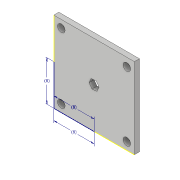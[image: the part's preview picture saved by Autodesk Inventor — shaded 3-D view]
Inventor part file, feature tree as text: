
AUTODESK INVENTOR PART (.ipt)
format: ipt  version: 2019 (Build 230136000, 136)  size: 120,320 bytes
history: native  units: in
note: dims shown in document units (in); Inventor stores cm internally (conversion verified against a paired STEP export)
features: sketch x5, extrude x3
ambient origin geometry x8: Origin, YZ Plane, XZ Plane, XY Plane, X Axis, Y Axis, Z Axis, Center Point
bodies: Solid1 (feature_tree)
feature tree (8):
  extrude  "Extrusion1"  Depth=6.2992in
  extrude  "Extrusion2"  Depth=0.3937in
  sketch  "Sketch3"  dims[d5=0.5906in d6=0.5906in]
  sketch  "Sketch4"  dims[d7=0.5906in]
  extrude  "Extrusion3"  Depth=0.5906in
  sketch  "Sketch1"  dims[d0=6.2992in d1=6.2992in]
  sketch  "Sketch2"  dims[d2=0.3937in d3=0.0in d4=0.5906in]
  sketch  "Sketch5"  dims[d8=0.5906in d9=0.6496in d10=0.5906in d11=0.5906in d12=0.5906in d13=0.5906in d14=0.5906in d15=0.5906in d16=0.3937in d17=0.0in d18=3.1496in d19=3.1496in d20=3.1496in d21=3.1496in d22=3.1496in d23=0.3937in d24=0.3937in d25=0.0in]
